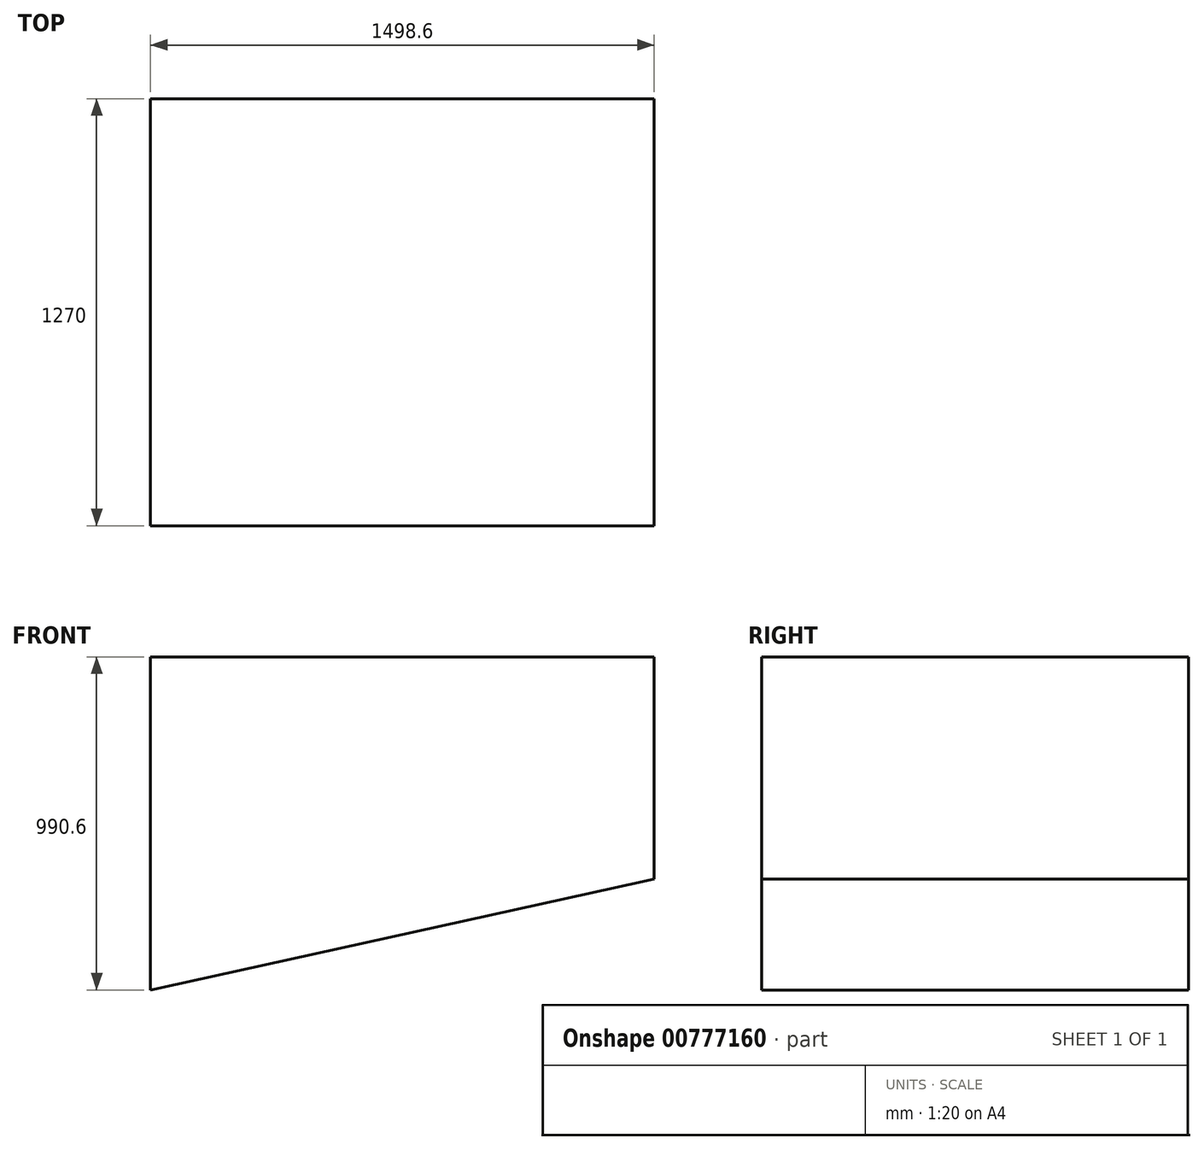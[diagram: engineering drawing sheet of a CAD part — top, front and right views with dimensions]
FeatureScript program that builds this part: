
annotation { "Feature Type Name" : "Feature", "Feature Type Description" : "" }
export const myFeature = defineFeature(function(context is Context, id is Id, definition is map)
    precondition{}
    {
        {
            var Q0;
            Q0=qCreatedBy(makeId("Front.planeOp"),FACE);
            var sketch = newSketch(context, id + "F0", { "sketchPlane" : qUnion([Q0])});
            skLineSegment(sketch, "E0", {"start": v(0, 0) * mm, "end": v(0, 990.6) * mm});
            skLineSegment(sketch, "E1", {"start": v(0, 990.6) * mm, "end": v(1498.6, 990.6) * mm});
            skLineSegment(sketch, "E2", {"start": v(1498.6, 990.6) * mm, "end": v(1498.6, 330.2) * mm});
            skLineSegment(sketch, "E3", {"start": v(1498.6, 330.2) * mm, "end": v(0, 0) * mm});
            skSolve(sketch);
        }
        {
            var Q0;
            Q0=makeQuery(id+"F0.imprint","IMPRINT",FACE,{"disambiguationData":[TD([[makeQuery(id+"F0.imprint","IMPRINT",EDGE,{"derivedFrom":sQuery(id+"F0.wireOp",EDGE,"E0")}),-1.0]])]});
            extrude(context, id + "F1", {"entities" : qUnion([Q0]), "depth" : 1270 * mm, "offsetDistance" : 25.4 * mm});
        }
    });
